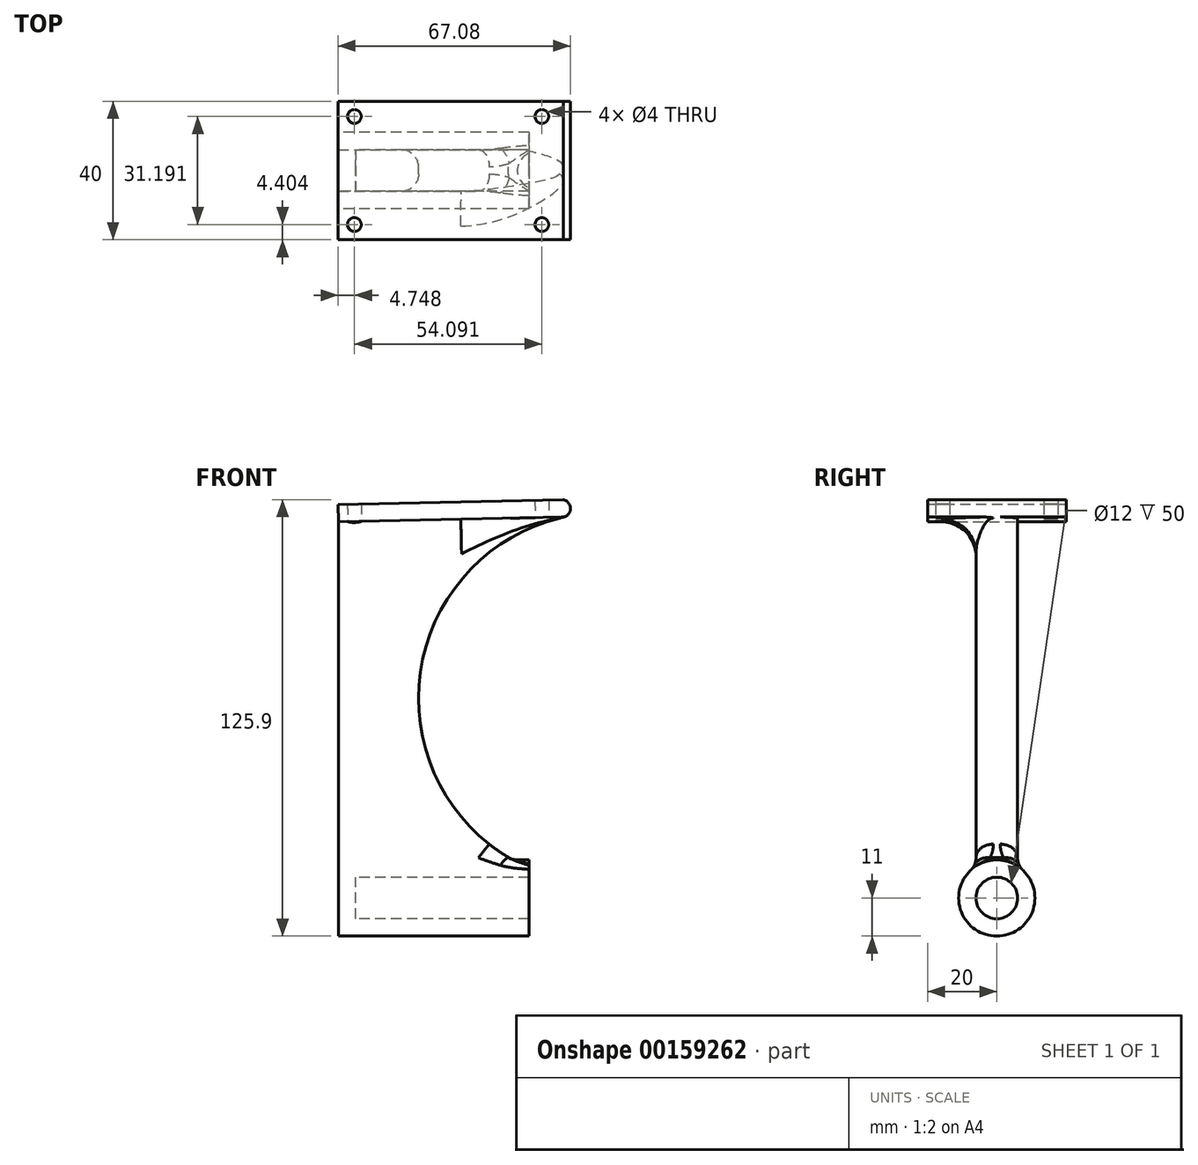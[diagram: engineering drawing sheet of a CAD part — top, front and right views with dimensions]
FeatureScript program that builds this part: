
annotation { "Feature Type Name" : "Feature", "Feature Type Description" : "" }
export const myFeature = defineFeature(function(context is Context, id is Id, definition is map)
    precondition{}
    {
        {
            var Q0;
            Q0=qCreatedBy(makeId("Right.planeOp"),FACE);
            var sketch = newSketch(context, id + "F0", { "sketchPlane" : qUnion([Q0])});
            skCircle(sketch, "E0", {"center": v(0, 0) * mm, "radius": 6 * mm});
            skCircle(sketch, "E1.0", {"center": v(0, 0) * mm, "radius": 11 * mm});
            skSolve(sketch);
        }
        {
            var Q0;
            Q0 = qSketchRegion(id + "F0", true);
            extrude(context, id + "F1", {"entities" : qUnion([Q0]), "depth" : 50 * mm});
        }
        {
            var Q0;
            Q0=makeQuery(id+"F1.opExtrude","CAP_FACE",FACE,{"disambiguationData":[OSD([sQuery(id+"F0.wireOp",EDGE,"E0"),sQuery(id+"F0.wireOp",EDGE,"E1.0")])],"isStart":true});
            var sketch = newSketch(context, id + "F2", { "sketchPlane" : qUnion([Q0])});
            skCircle(sketch, "E2.0", {"center": v(0, 0) * mm, "radius": 11 * mm});
            skSolve(sketch);
        }
        {
            var Q0;
            Q0 = qSketchRegion(id + "F2", true);
            extrude(context, id + "F3", {"entities" : qUnion([Q0]), "operationType" : NewBodyOperationType.ADD, "depth" : 5 * mm});
        }
        {
            var Q0;
            Q0=qCreatedBy(makeId("Top.planeOp"),FACE);
            cPlane(context, id + "F4", {"entities" : qUnion([Q0]), "cplaneType" : CPlaneType.OFFSET, "offset" : 8.5 * mm, "width" : 150 * mm, "height" : 150 * mm});
        }
        {
            var Q0;
            Q0=qCreatedBy(makeId("Front.planeOp"),FACE);
            var sketch = newSketch(context, id + "F5", { "sketchPlane" : qUnion([Q0])});
            skPoint(sketch, "E3.start.orphan", {"position": v(0, 13.88) * mm});
            skLineSegment(sketch, "E4", {"start": v(-4.98, 8.54) * mm, "end": v(50, 8.62) * mm});
            skLineSegment(sketch, "E5", {"start": v(-4.98, 108.54) * mm, "end": v(60, 109.9) * mm});
            skArc(sketch, "E6", {"start": v(60, 109.9) * mm, "mid": v(18.41, 62.88) * mm, "end": v(50, 8.62) * mm});
            skLineSegment(sketch, "E7", {"start": v(-4.98, 8.54) * mm, "end": v(-4.98, 108.54) * mm});
            skPoint(sketch, "E8.orphan", {"position": v(0, 8.55) * mm});
            skSolve(sketch);
        }
        {
            var Q0;
            Q0 = qSketchRegion(id + "F5", true);
            extrude(context, id + "F6", {"entities" : qUnion([Q0]), "operationType" : NewBodyOperationType.ADD, "endBound" : BoundingType.SYMMETRIC, "depth" : 12 * mm});
        }
        {
            var Q0;
            Q0=makeQuery(id+"F6.opExtrude","SWEPT_FACE",FACE,{"disambiguationData":[OSD([sQuery(id+"F5.wireOp",EDGE,"E5")])]});
            var sketch = newSketch(context, id + "F7", { "sketchPlane" : qUnion([Q0])});
            skLineSegment(sketch, "E9", {"start": v(0, 0) * mm, "end": v(-52.31, 0) * mm, "construction": true});
            skLineSegment(sketch, "E10.bottom", {"start": v(62.3, 20) * mm, "end": v(-2.7, 20) * mm});
            skLineSegment(sketch, "E10.top", {"start": v(62.3, -20) * mm, "end": v(-2.7, -20) * mm});
            skLineSegment(sketch, "E10.left", {"start": v(62.3, 20) * mm, "end": v(62.3, -20) * mm});
            skLineSegment(sketch, "E10.right", {"start": v(-2.7, 20) * mm, "end": v(-2.7, -20) * mm});
            skPoint(sketch, "E10.middle", {"position": v(29.8, 0) * mm});
            skLineSegment(sketch, "E11.0", {"start": v(-2.7, -6) * mm, "end": v(-2.7, 6) * mm, "construction": true});
            skSolve(sketch);
        }
        {
            var Q0;
            Q0=makeQuery(id+"F6.boolean.opBoolean","INTERSECT",EDGE,{"derivedFrom":[makeQuery(id+"F3.boolean.opBoolean","MERGE",FACE,{"derivedFrom":[makeQuery(id+"F1.opExtrude","SWEPT_FACE",FACE,{"disambiguationData":[OSD([sQuery(id+"F0.wireOp",EDGE,"E1.0")])]}),makeQuery(id+"F3.opExtrude","SWEPT_FACE",FACE,{"disambiguationData":[OSD([sQuery(id+"F2.wireOp",EDGE,"E2.0")])]})]}),makeQuery(id+"F6.opExtrude","CAP_FACE",FACE,{"disambiguationData":[OSD([sQuery(id+"F5.wireOp",EDGE,"jmuqxTvc-2utY-pKSh-sO6E-nQKjDO1EMLVv"),sQuery(id+"F5.wireOp",EDGE,"E4"),sQuery(id+"F5.wireOp",EDGE,"zIHVAkZa-mPjm-NHBF-WN69-n4djU8HBVBrq"),sQuery(id+"F5.wireOp",EDGE,"bfE9QwAt-4JC9-C8Fi-lR3f-WzyjK1qeIF5V")])],"isStart":true})]});
            var Q1;
            Q1=makeQuery(id+"F6.boolean.opBoolean","INTERSECT",EDGE,{"derivedFrom":[makeQuery(id+"F3.boolean.opBoolean","MERGE",FACE,{"derivedFrom":[makeQuery(id+"F1.opExtrude","SWEPT_FACE",FACE,{"disambiguationData":[OSD([sQuery(id+"F0.wireOp",EDGE,"E1.0")])]}),makeQuery(id+"F3.opExtrude","SWEPT_FACE",FACE,{"disambiguationData":[OSD([sQuery(id+"F2.wireOp",EDGE,"E2.0")])]})]}),makeQuery(id+"F6.opExtrude","SWEPT_FACE",FACE,{"disambiguationData":[OSD([sQuery(id+"F5.wireOp",EDGE,"jmuqxTvc-2utY-pKSh-sO6E-nQKjDO1EMLVv")])]})]});
            var Q2;
            Q2=makeQuery(id+"F6.boolean.opBoolean","INTERSECT",EDGE,{"derivedFrom":[makeQuery(id+"F3.boolean.opBoolean","MERGE",FACE,{"derivedFrom":[makeQuery(id+"F1.opExtrude","SWEPT_FACE",FACE,{"disambiguationData":[OSD([sQuery(id+"F0.wireOp",EDGE,"E1.0")])]}),makeQuery(id+"F3.opExtrude","SWEPT_FACE",FACE,{"disambiguationData":[OSD([sQuery(id+"F2.wireOp",EDGE,"E2.0")])]})]}),makeQuery(id+"F6.opExtrude","CAP_FACE",FACE,{"disambiguationData":[OSD([sQuery(id+"F5.wireOp",EDGE,"jmuqxTvc-2utY-pKSh-sO6E-nQKjDO1EMLVv"),sQuery(id+"F5.wireOp",EDGE,"E4"),sQuery(id+"F5.wireOp",EDGE,"zIHVAkZa-mPjm-NHBF-WN69-n4djU8HBVBrq"),sQuery(id+"F5.wireOp",EDGE,"bfE9QwAt-4JC9-C8Fi-lR3f-WzyjK1qeIF5V")])],"isStart":false})]});
            fillet(context, id + "F8", {"entities" : qUnion([Q0, Q1, Q2]), "radius" : 5 * mm, "tangentPropagation" : true, "allowEdgeOverflow" : false});
        }
        {
            var Q0;
            Q0 = qSketchRegion(id + "F7", true);
            extrude(context, id + "F9", {"entities" : qUnion([Q0]), "operationType" : NewBodyOperationType.ADD, "depth" : 5 * mm});
        }
        {
            var Q0;
            Q0=qCreatedBy(makeId("Front.planeOp"),FACE);
            var sketch = newSketch(context, id + "F10", { "sketchPlane" : qUnion([Q0])});
            skLineSegment(sketch, "E12.0", {"start": v(59.9, 114.9) * mm, "end": v(-5.08, 113.54) * mm, "construction": true});
            skLineSegment(sketch, "E13", {"start": v(59.9, 114.9) * mm, "end": v(59.85, 114.9) * mm});
            skPoint(sketch, "E14.0.start.orphan", {"position": v(31.49, 91.06) * mm});
            skArc(sketch, "E15.0", {"start": v(60, 109.9) * mm, "mid": v(18.83, 66.1) * mm, "end": v(44.22, 11.62) * mm, "construction": true});
            skArc(sketch, "E16", {"start": v(60, 109.9) * mm, "mid": v(62, 112.44) * mm, "end": v(59.9, 114.9) * mm});
            skLineSegment(sketch, "E17", {"start": v(59.85, 114.9) * mm, "end": v(60, 109.9) * mm});
            skSolve(sketch);
        }
        {
            var Q0;
            Q0 = qSketchRegion(id + "F10", true);
            extrude(context, id + "F11", {"entities" : qUnion([Q0]), "operationType" : NewBodyOperationType.ADD, "endBound" : BoundingType.SYMMETRIC, "depth" : 40 * mm});
        }
        {
            var Q0;
            Q0=makeQuery(id+"F6.opExtrude","SWEPT_FACE",FACE,{"disambiguationData":[OSD([sQuery(id+"F5.wireOp",EDGE,"E6")])]});
            fillet(context, id + "F12", {"entities" : qUnion([Q0]), "radius" : 5 * mm, "tangentPropagation" : true, "allowEdgeOverflow" : false});
        }
        {
            var Q0;
            {var subQ0=sQuery(id+"F7.wireOp",EDGE,"E10.bottom");var subQ3=sQuery(id+"F7.wireOp",EDGE,"E10.left");var subQ4=sQuery(id+"F7.wireOp",EDGE,"E10.right");Q0=makeQuery(id+"F9.boolean.opBoolean","SPLIT",FACE,{"disambiguationData":[TD([makeQuery(id+"F9.opExtrude","SWEPT_FACE",FACE,{"disambiguationData":[OSD([subQ0])]})])],"derivedFrom":makeQuery(id+"F9.opExtrude","CAP_FACE",FACE,{"disambiguationData":[OSD([subQ0,sQuery(id+"F7.wireOp",EDGE,"E10.top"),subQ3,subQ4])],"isStart":true})});}
            var sketch = newSketch(context, id + "F13", { "sketchPlane" : qUnion([Q0])});
            skCircle(sketch, "E18", {"center": v(56.1, 15.6) * mm, "radius": 2 * mm});
            skCircle(sketch, "E19.MirrorC", {"center": v(56.1, -15.6) * mm, "radius": 2 * mm});
            skPoint(sketch, "E20.center.orphan", {"position": v(0, 15.6) * mm});
            skPoint(sketch, "E21.MirrorC.center.orphan", {"position": v(0, -15.6) * mm});
            skCircle(sketch, "E22", {"center": v(2, -15.6) * mm, "radius": 2 * mm});
            skCircle(sketch, "E23", {"center": v(2, 15.6) * mm, "radius": 2 * mm});
            skSolve(sketch);
        }
        {
            var Q0;
            Q0 = qSketchRegion(id + "F13", true);
            extrude(context, id + "F14", {"entities" : qUnion([Q0]), "operationType" : NewBodyOperationType.REMOVE, "endBound" : BoundingType.THROUGH_ALL, "oppositeDirection" : true, "depth" : 25 * mm});
        }
        {
            var Q0;
            Q0=makeQuery(id+"F6.opExtrude","CAP_EDGE",EDGE,{"disambiguationData":[OSD([sQuery(id+"F5.wireOp",EDGE,"E5")])],"isStart":true});
            var Q1;
            Q1=makeQuery(id+"F6.opExtrude","CAP_EDGE",EDGE,{"disambiguationData":[OSD([sQuery(id+"F5.wireOp",EDGE,"E5")])],"isStart":false});
            fillet(context, id + "F15", {"entities" : qUnion([Q0, Q1]), "radius" : 10 * mm, "tangentPropagation" : true, "allowEdgeOverflow" : false});
        }
    });
